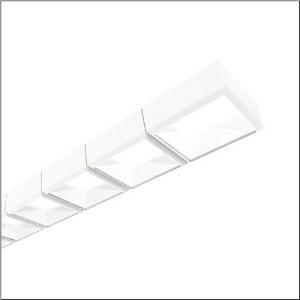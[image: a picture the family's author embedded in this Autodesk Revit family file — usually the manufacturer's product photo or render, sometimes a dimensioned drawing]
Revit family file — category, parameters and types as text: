
# Revit family: scriptus_11_5mz314d0twb
name_source: partatom
category: Lighting Fixtures
units: mm (PartAtom-declared; Revit-internal decimal feet)

## family parameters
Cut with Voids When Loaded = No
Host = Face
Light Source = No
Part Type = Normal
Room Calculation Point = No
Round Connector Dimension = Use Diameter
Shared = No

## types (1)
- --- (1 x LED 3000K+6500K / CRI = 80 (unbekannt), 3390 lm / 3600 lm, 3000K)
    Apparent Load = 106 VA
    CIE Flux Codes = 0 0 0 0 100 / 82 95 99 100 100
    Color Rendering = 80
    Color Temperature = 3000K
    Default Elevation = 1800 mm
    Description = Scriptus 11, office luminaire, primary optical cover: lenses, CAT 2 (L<= 3000cd/m²), light emission: direct/indirect distribution, primary light characteristic: symmetric, installation type: suspended mounting, LED, rated luminous flux: 13.970lm, luminous efficacy: 128lm/W, light colour: 8tw, colour temperature: 3000..6500K, control gear: DALI DT8, with terminal, 5-pole, mains connection: 230V, AC, 50Hz, rated input power: 110W, LED, control gear: ECG DALI, housing, luminaire housing, of aluminium, traffic white (RAL 9016), length: 3.088mm, width: 114mm, height: 57mm, protection rating (complete): IP20, insulation class (complete): insulation class I (protective earthing), certification: CE, protection symbol: F, permissible operating ambient temperature: <= +25°C, standard: EN 50419, packaging unit: 1 piece
    Height = 57 mm
    Lamp = 1 x LED 3000K+6500K / CRI >= 80 (unbekannt)
    Lamp Light Flux = 3390 lm / 3600 lm
    Lamp count = 1
    Length = 3088 mm
    Luminous efficacy = 132 lm/W
    Manufacturer = Siteco
    ModVariant = No
    Model = 5MZ314D0TWB
    Mounting Place = Ceiling
    Mounting Type = Pendant
    Number of Poles = 1
    OnlyDefault = Yes
    Power Factor = 1
    Product Name = Scriptus 11
    Product group = office luminaire | ceiling pendant
    ProductGroupID = 903
    Protection Class = Protection class I
    Protection Degree = IP 20
    RLX_Detail_Level = 1
    RLX_Emergency_Light_Flux = 0 lm
    RLX_Emergency_Type = 0
    RLX_Emergency_Type_DB = No
    RlxData = <blob elided: 32301 chars, md5=569e00ba>
    Socket = socket
    Standby Power = 0 W
    System Light Flux = 13980 lm
    System Power = 106 W
    Type Comments = individual setting: colour temperature 6500K
    Type Image = l_1004839.jpg
    URL = http://relux.com
    VarID = @adj_196170
    Voltage = 0 V
    Weight = 0.00 kg
    Width = 114 mm

## geometry (parser evidence)
native form markers: Blend x4, Sweep x19
no freeform markers — native parametric forms only
